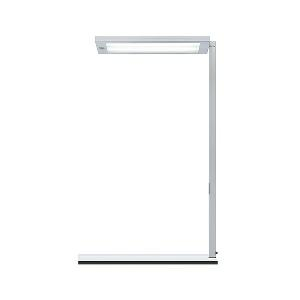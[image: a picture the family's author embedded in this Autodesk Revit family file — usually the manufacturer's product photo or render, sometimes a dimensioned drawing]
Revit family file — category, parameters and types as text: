
# Revit family: lavigo_-_dpt_14000_840_d_g2_00807262_ea04
name_source: partatom
category: Lighting Fixtures
units: mm (PartAtom-declared; Revit-internal decimal feet)

## family parameters
Cut with Voids When Loaded = No
Host = Face
Light Source = No
Part Type = Normal
Room Calculation Point = No
Round Connector Dimension = Use Diameter
Shared = No

## types (1)
- LAVIGO - DPT 14000/840/D/G2 (1 x LED, 14050 lm, 4000K)
    Apparent Load = 93 VA
    Approval mark = CE
    CIE Flux Codes = 60 87 97 12 100
    Color Rendering = 80-89
    Color Temperature = 4000K
    Control Gear = Electronic ballast
    Default Elevation = 1800 mm
    Description = DPT 14000/840/D/G2|Desk-mounted luminaire|light source: LED|work equipment: Electronic ballast|connected load: 220-240 V, 50/60 Hz|Power consumption: approx. 93 W|standby: approx. 0,50|power factor: approx. 0,943|luminous flux: 14050 lm|luminous efficacy: 151 lm/W|light distribution: Direct/indirect|direct ratio: approx. 12 %|colour temperature: Cold white, ca. 4000 K|color rendering index (CRI): >= 80|chromaticity tolerance:  3 SDCM|technology: Continuously dimmable|operation: Multi-function switch|luminaire body|material: Steel/plastic|surface: Painted|colour: White|lamp cover: Acrylic (PMMA), Satine|tubular section|material: Steel tube|surface: Painted|Form: Tubular section upright|colour of tubular section: White|weight (net): approx. 9.5 kg|mains lead: 3.70 m Mains plug CEE 7/VII|Fastening: Socket, Table adaptor|decorative contrast side parts: Flint grey|glare control: Prism aperture|luminance(L65): <= 3000 cd/m|unified glare rating(4H 8H): <=  16|special features: Luminaire head detachable, Cradle to Cradle Certified TM, Direct light component with edge light and light-guide technology for homogenous light exit, Flicker-free, Inclination of tubular section adjustable, Separated, direct and indirect light individually adjustable|
    Frequency = 50 Hz, 60 Hz
    Height = 36 mm
    Lamp = 1 x LED
    Lamp Light Flux = 14050 lm
    Lamp count = 1
    Length = 675 mm
    Luminous efficacy = 151 lm/W
    Manufacturer = Waldmann
    ModVariant = No
    Model = 00807262
    Mounting Place = Table
    Mounting Type = Surface mounted
    Number of Poles = 1
    OnlyDefault = Yes
    Power Factor = 1
    Product Name = LAVIGO - DPT 14000/840/D/G2
    Product group = Desk mounted luminaire
    ProductGroupID = 22
    Protection Class = Protection class I
    Protection Degree = IP 20
    RLX_Detail_Level = 1
    RLX_Emergency_Light_Flux = 0 lm
    RLX_Emergency_Type = 0
    RLX_Emergency_Type_DB = No
    RlxData = <blob elided: 34801 chars, md5=4bb41efc>
    Socket = socket
    Standby Power = 0 W
    System Light Flux = 14050 lm
    System Power = 93 W
    Type Comments = Product without accessories
    Type Image = 121716000-00630762.jpg
    URL = http://relux.com
    VarID = ---
    Voltage = 230 V
    Voltage Range = 220-240 V
    Weight = 0.00 kg
    Width = 320 mm

## geometry (parser evidence)
native form markers: Blend x4, Sweep x15
no freeform markers — native parametric forms only
